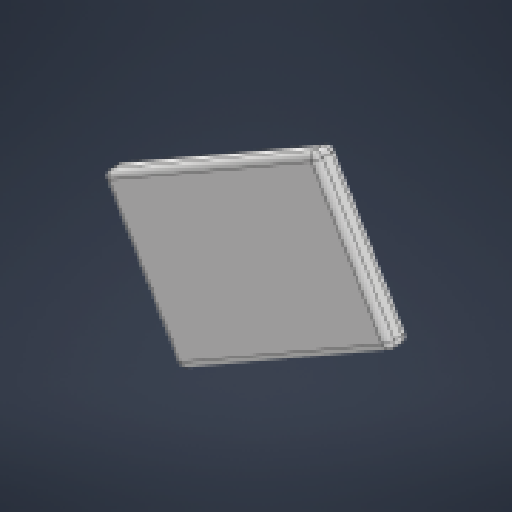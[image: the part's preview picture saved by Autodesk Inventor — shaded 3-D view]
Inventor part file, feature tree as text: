
AUTODESK INVENTOR PART (.ipt)
format: ipt  version: 2023 (Build 270158000, 158)  size: 144,896 bytes
history: native  units: in
note: dims shown in document units (in); Inventor stores cm internally (conversion verified against a paired STEP export)
features: extrude x1, fillet x1, sketch x1
ambient origin geometry x8: Origin, YZ Plane, XZ Plane, XY Plane, X Axis, Y Axis, Z Axis, Center Point
bodies: Solid1 (feature_tree)
feature tree (3):
  extrude  "Extrusion1"  TaperAngle=30.0deg  [1 undecoded]
  fillet  "Fillet1"  Radius=0.7283in
  sketch  "Sketch1"  dims[d0=1.1614in d1=30.0deg d2=0.7283in d3=0.1969in d4=0.0in d5=0.0591in]
note: 1 required parameter value undecoded (feature->parameter linkage not recoverable at this tier; creation-order binding heuristic only, values carry confidence <= 0.55)
